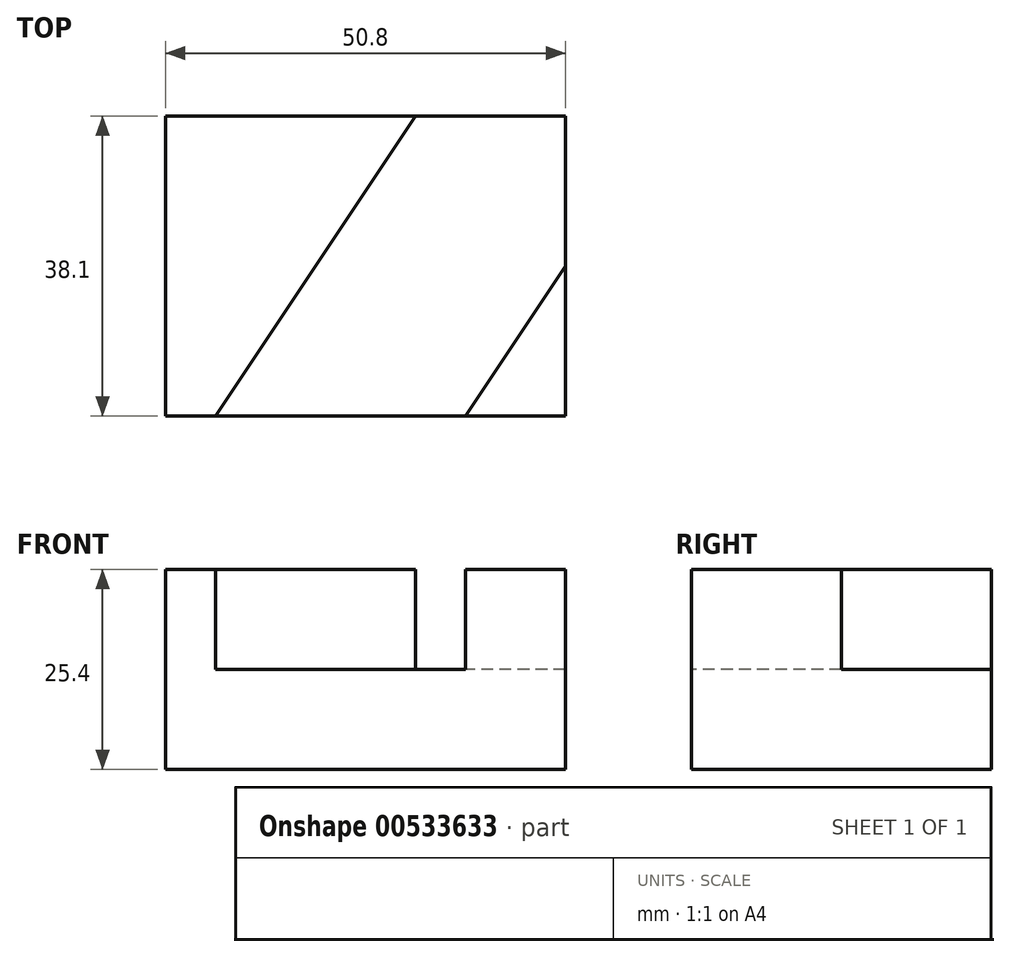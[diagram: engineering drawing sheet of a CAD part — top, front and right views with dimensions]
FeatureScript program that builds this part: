
annotation { "Feature Type Name" : "Feature", "Feature Type Description" : "" }
export const myFeature = defineFeature(function(context is Context, id is Id, definition is map)
    precondition{}
    {
        {
            var Q0;
            Q0=qCreatedBy(makeId("Top.planeOp"),FACE);
            var sketch = newSketch(context, id + "F0", { "sketchPlane" : qUnion([Q0])});
            skLineSegment(sketch, "E0", {"start": v(-21.07, 14.82) * mm, "end": v(-21.07, -23.28) * mm});
            skLineSegment(sketch, "E1", {"start": v(-21.07, -23.28) * mm, "end": v(29.73, -23.28) * mm});
            skLineSegment(sketch, "E2", {"start": v(29.73, -23.28) * mm, "end": v(29.73, 14.82) * mm});
            skLineSegment(sketch, "E3", {"start": v(29.73, 14.82) * mm, "end": v(-21.07, 14.82) * mm});
            skSolve(sketch);
        }
        {
            var Q0;
            Q0=makeQuery(id+"F0.imprint","IMPRINT",FACE,{"disambiguationData":[TD([[makeQuery(id+"F0.imprint","IMPRINT",EDGE,{"derivedFrom":sQuery(id+"F0.wireOp",EDGE,"E0")}),1.0]])]});
            extrude(context, id + "F1", {"entities" : qUnion([Q0]), "depth" : 25.4 * mm, "offsetDistance" : 25.4 * mm});
        }
        {
            var Q0;
            Q0=makeQuery(id+"F1.opExtrude","CAP_FACE",FACE,{"disambiguationData":[OSD([sQuery(id+"F0.wireOp",EDGE,"E0"),sQuery(id+"F0.wireOp",EDGE,"E1"),sQuery(id+"F0.wireOp",EDGE,"E2"),sQuery(id+"F0.wireOp",EDGE,"E3")])],"isStart":false});
            var sketch = newSketch(context, id + "F2", { "sketchPlane" : qUnion([Q0])});
            skLineSegment(sketch, "E4", {"start": v(29.73, -4.23) * mm, "end": v(17.03, -23.28) * mm});
            skLineSegment(sketch, "E5", {"start": v(17.03, -23.28) * mm, "end": v(-14.72, -23.28) * mm});
            skLineSegment(sketch, "E6", {"start": v(-14.72, -23.28) * mm, "end": v(10.68, 14.82) * mm});
            skSolve(sketch);
        }
        {
            var Q0;
            {var subQ3=sQuery(id+"F2.wireOp",EDGE,"E4");Q0=makeQuery(id+"F2.imprint","IMPRINT",FACE,{"disambiguationData":[TD([[makeQuery(id+"F2.imprint","IMPRINT",EDGE,{"derivedFrom":subQ3}),-1.0]])]});}
            extrude(context, id + "F3", {"entities" : qUnion([Q0]), "operationType" : NewBodyOperationType.REMOVE, "oppositeDirection" : true, "depth" : 12.7 * mm, "offsetDistance" : 25.4 * mm});
        }
    });
